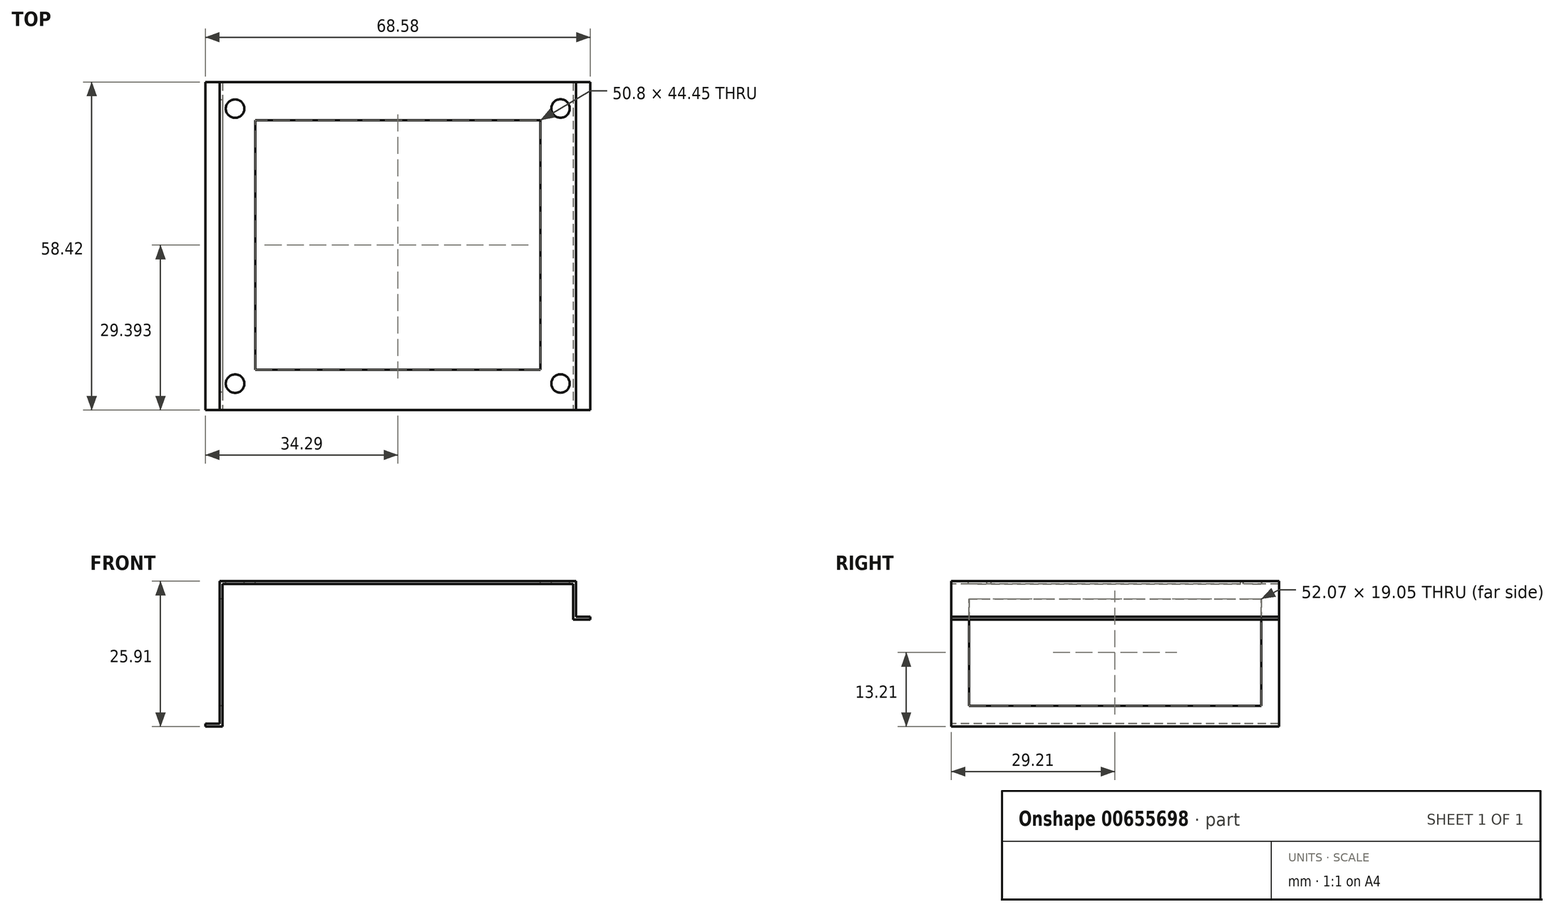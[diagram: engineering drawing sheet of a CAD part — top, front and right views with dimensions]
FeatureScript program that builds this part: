
annotation { "Feature Type Name" : "Feature", "Feature Type Description" : "" }
export const myFeature = defineFeature(function(context is Context, id is Id, definition is map)
    precondition{}
    {
        {
            var Q0;
            Q0=qCreatedBy(makeId("Front.planeOp"),FACE);
            var sketch = newSketch(context, id + "F0", { "sketchPlane" : qUnion([Q0])});
            skLineSegment(sketch, "E0", {"start": v(0, 0) * mm, "end": v(63.5, 0) * mm});
            skLineSegment(sketch, "E1", {"start": v(63.5, 0) * mm, "end": v(63.5, -6.35) * mm});
            skLineSegment(sketch, "E2", {"start": v(63.5, -6.35) * mm, "end": v(66.04, -6.35) * mm});
            skLineSegment(sketch, "E3", {"start": v(0, 0) * mm, "end": v(0, -25.4) * mm});
            skLineSegment(sketch, "E4", {"start": v(0, -25.4) * mm, "end": v(-2.54, -25.4) * mm});
            skLineSegment(sketch, "E5", {"start": v(-2.54, -25.4) * mm, "end": v(-2.54, -25.9) * mm});
            skLineSegment(sketch, "E6", {"start": v(-2.54, -25.9) * mm, "end": v(0.5, -25.9) * mm});
            skLineSegment(sketch, "E7", {"start": v(0.5, -25.9) * mm, "end": v(0.5, -0.5) * mm});
            skLineSegment(sketch, "E8", {"start": v(0.5, -0.5) * mm, "end": v(63, -0.5) * mm});
            skLineSegment(sketch, "E9", {"start": v(63, -0.5) * mm, "end": v(63, -6.86) * mm});
            skLineSegment(sketch, "E10", {"start": v(63, -6.86) * mm, "end": v(66.04, -6.86) * mm});
            skLineSegment(sketch, "E11", {"start": v(66.04, -6.86) * mm, "end": v(66.04, -6.35) * mm});
            skLineSegment(sketch, "E12", {"start": v(0.5, -25.9) * mm, "end": v(63, -6.86) * mm, "construction": true});
            skSolve(sketch);
        }
        {
            var Q0;
            Q0=makeQuery(id+"F0.imprint","IMPRINT",FACE,{"disambiguationData":[TD([[makeQuery(id+"F0.imprint","IMPRINT",EDGE,{"derivedFrom":sQuery(id+"F0.wireOp",EDGE,"E0")}),-1.0]])]});
            var Q1;
            Q1=makeQuery(id+"F0.imprint","IMPRINT",FACE,{"disambiguationData":[TD([[makeQuery(id+"F0.imprint","IMPRINT",EDGE,{"derivedFrom":sQuery(id+"F0.wireOp",EDGE,"E7")}),-1.0]])]});
            extrude(context, id + "F1", {"entities" : qUnion([Q0, Q1]), "oppositeDirection" : true, "depth" : 58.42 * mm, "offsetDistance" : 25.4 * mm});
        }
        {
            var Q0;
            Q0=makeQuery(id+"F1.opExtrude","SWEPT_FACE",FACE,{"disambiguationData":[OSD([sQuery(id+"F0.wireOp",EDGE,"E0")])]});
            var sketch = newSketch(context, id + "F2", { "sketchPlane" : qUnion([Q0])});
            skCircle(sketch, "E13", {"center": v(2.76, 53.7) * mm, "radius": 1.65 * mm});
            skCircle(sketch, "E14", {"center": v(2.76, 4.7) * mm, "radius": 1.65 * mm});
            skCircle(sketch, "E15", {"center": v(60.74, 53.72) * mm, "radius": 1.65 * mm});
            skCircle(sketch, "E16", {"center": v(60.74, 4.72) * mm, "radius": 1.65 * mm});
            skSolve(sketch);
        }
        {
            var Q0;
            Q0 = qSketchRegion(id + "F2", true);
            extrude(context, id + "F3", {"entities" : qUnion([Q0]), "operationType" : NewBodyOperationType.REMOVE, "oppositeDirection" : true, "depth" : 25.4 * mm, "offsetDistance" : 25.4 * mm});
        }
        {
            var Q0;
            Q0=makeQuery(id+"F1.opExtrude","SWEPT_FACE",FACE,{"disambiguationData":[OSD([sQuery(id+"F0.wireOp",EDGE,"E0")])]});
            var sketch = newSketch(context, id + "F4", { "sketchPlane" : qUnion([Q0])});
            skLineSegment(sketch, "E17.bottom", {"start": v(57.15, 51.62) * mm, "end": v(6.35, 51.62) * mm});
            skLineSegment(sketch, "E17.top", {"start": v(57.15, 7.17) * mm, "end": v(6.35, 7.17) * mm});
            skLineSegment(sketch, "E17.left", {"start": v(57.15, 51.62) * mm, "end": v(57.15, 7.17) * mm});
            skLineSegment(sketch, "E17.right", {"start": v(6.35, 51.62) * mm, "end": v(6.35, 7.17) * mm});
            skPoint(sketch, "E17.middle", {"position": v(31.75, 29.4) * mm});
            skSolve(sketch);
        }
        {
            var Q0;
            Q0 = qSketchRegion(id + "F4", true);
            extrude(context, id + "F5", {"entities" : qUnion([Q0]), "operationType" : NewBodyOperationType.REMOVE, "endBound" : BoundingType.THROUGH_ALL, "oppositeDirection" : true, "depth" : 25.4 * mm, "offsetDistance" : 25.4 * mm});
        }
        {
            var Q0;
            Q0=makeQuery(id+"F1.opExtrude","SWEPT_FACE",FACE,{"disambiguationData":[OSD([sQuery(id+"F0.wireOp",EDGE,"E3")])]});
            var sketch = newSketch(context, id + "F6", { "sketchPlane" : qUnion([Q0])});
            skLineSegment(sketch, "E18.bottom", {"start": v(-3.17, -22.22) * mm, "end": v(-55.25, -22.23) * mm});
            skLineSegment(sketch, "E18.top", {"start": v(-3.18, -3.17) * mm, "end": v(-55.25, -3.18) * mm});
            skLineSegment(sketch, "E18.left", {"start": v(-3.17, -22.22) * mm, "end": v(-3.18, -3.17) * mm});
            skLineSegment(sketch, "E18.right", {"start": v(-55.25, -22.23) * mm, "end": v(-55.25, -3.18) * mm});
            skPoint(sketch, "E18.middle", {"position": v(-29.21, -12.7) * mm});
            skSolve(sketch);
        }
        {
            var Q0;
            Q0 = qSketchRegion(id + "F6", true);
            extrude(context, id + "F7", {"entities" : qUnion([Q0]), "operationType" : NewBodyOperationType.REMOVE, "oppositeDirection" : true, "depth" : 25.4 * mm, "offsetDistance" : 25.4 * mm});
        }
    });
